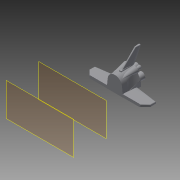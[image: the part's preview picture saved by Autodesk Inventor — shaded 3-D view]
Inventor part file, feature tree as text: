
AUTODESK INVENTOR PART (.ipt)
format: ipt  version: 2015 (Build 190159000, 159)  size: 1,837,568 bytes
history: native  units: in
note: dims shown in document units (in); Inventor stores cm internally (conversion verified against a paired STEP export)
features: sketch x29, plane x15, loft x11, extrude x9, fillet x6, other x3, projected_geometry x3, mirror x2, chamfer x2
ambient origin geometry x8: Origin, YZ Plane, XZ Plane, XY Plane, X Axis, Y Axis, Z Axis, Center Point
bodies: Solid1 (feature_tree)
feature tree (80):
  extrude  "Extrusion1"  TaperAngle=0.0deg  [1 undecoded]
  plane  "Work Plane1"
  plane  "Work Plane2"
  plane  "Work Plane3"
  loft  "Loft1"
  loft  "Loft2"
  fillet  "Fillet1"  Radius=240.6614in
  loft  "Loft4"
  fillet  "Fillet2"  Radius=125.0in
  extrude  "Extrusion2"  TaperAngle=0.0deg  [1 undecoded]
  extrude  "Extrusion3"  Depth=100.0in
  fillet  "Fillet3"  [1 undecoded]
  plane  "Work Plane4"
  mirror  "Mirror1"
  plane  "Work Plane5"
  sketch  "Sketch12"  dims[d36=0.0in d37=90.0deg d38=125.0in]
  loft  "Loft5"
  chamfer  "Chamfer1"  Angle=90.0deg  [1 undecoded]
  chamfer  "Chamfer2"  Angle=90.0deg  [1 undecoded]
  sketch  "Sketch15"  dims[d39=15.0in]
  plane  "Work Plane6"
  plane  "Work Plane7"
  loft  "Loft8"
  mirror  "Mirror2"
  extrude  "Extrusion5"  Depth=125.0in
  extrude  "Extrusion6"  TaperAngle=0.0deg  [1 undecoded]
  plane  "Work Plane8"
  sketch  "Sketch20"  dims[d51=10.0in]
  plane  "Work Plane10"
  loft  "Loft9"
  fillet  "Fillet4"  Radius=84.0in
  extrude  "Extrusion7"  Depth=0.6803in
  fillet  "Fillet5"  Radius=48.0in
  fillet  "Fillet6"  Radius=6500.0in
  sketch  "Sketch23"  dims[d55=0.0in]
  plane  "Work Plane11"
  sketch  "Sketch24"  dims[d56=0.0in]
  loft  "Loft10"
  loft  "Loft11"
  sketch  "Sketch27"  dims[d64=60.0in d70=125.0in]
  plane  "Work Plane12"
  loft  "Loft12"
  loft  "Loft13"
  loft  "Loft14"
  sketch  "Sketch31"  dims[d89=6500.0in d90=7700.0in]
  plane  "Work Plane13"
  sketch  "Sketch32"  dims[d91=10.0in d92=345.0in d93=0.0in]
  sketch  "Sketch33"  dims[d94=10.0in d95=125.0in]
  plane  "Work Plane14"
  extrude  "Extrusion8"  Depth=245.0in
  sketch  "Sketch35"  dims[d98=10.0in d99=0.0in]
  plane  "Work Plane15"
  extrude  "Extrusion9"  Depth=15.0in
  plane  "Work Plane16"
  extrude  "Extrusion10"  Depth=0.0618in
  sketch  "Sketch1"  dims[d5=250.0in d12=0.0in]
  sketch  "Sketch2"  dims[d13=75.0in d15=110.0in]
  other  "Edges1"
  sketch  "Sketch3"  dims[d21=98.0in d24=110.0in d25=240.6614in]
  sketch  "Sketch6"  dims[d26=730.0in d27=0.0in d28=300.0in d29=125.0in]
  sketch  "Sketch7"  dims[d30=250.0in d31=0.0in]
  other  "Edges3"
  sketch  "Sketch8"  dims[d32=125.0in d33=100.0in d34=0.0in d35=90.0deg]
  other  "Edges4"
  sketch  "Sketch17"  dims[d40=20.0in]
  sketch  "Sketch18"  dims[d41=10.0in]
  sketch  "Sketch19"  dims[d50=15.0in]
  projected_geometry  "Projected Loop7"
  sketch  "Sketch21"  dims[d52=75.0in]
  sketch  "Sketch22"  dims[d54=125.0in]
  sketch  "Sketch25"  dims[d57=0.0in d58=0.0in d59=90.0deg d60=0.0in d61=90.0deg]
  sketch  "Sketch26"  dims[d62=10.65in d63=50.0in]
  sketch  "Sketch28"  dims[d71=50.0in d72=0.0in d73=90.0deg]
  sketch  "Sketch29"  dims[d74=0.0in d75=90.0deg d76=40.0in d79=84.0in]
  sketch  "Sketch30"  dims[d80=0.0in d82=0.6803in d83=48.0in d84=0.0in d85=6500.0in]
  sketch  "Sketch34"  dims[d96=200.0in d97=0.0in]
  projected_geometry  "Projected Loop8"
  projected_geometry  "Projected Loop9"
  sketch  "Sketch36"  dims[d100=0.0in d101=245.0in]
  sketch  "Sketch37"  dims[d102=90.0in d105=15.0in d106=0.0618in d107=45.0deg d108=345.0in d109=0.0in d110=90.0deg d111=0.0in d112=90.0deg d113=5.2in d114=0.125in d115=45.0deg d116=5.2in d117=0.125in d118=45.0deg d119=-200.0in d126=100.0in d127=25.0in d133=-205.0in d134=50.0in d135=60.0in d137=0.0in d138=90.0deg d139=0.0in d140=90.0deg d141=160.0in d142=100.0in d143=0.6528in d144=0.0in d145=0.0in d146=9000.0in d147=0.0in d148=15.0in d149=25.0in d150=0.0in d151=30.0in d152=0.0in d153=-20.0in d154=30.0in d155=10.0in d156=1.2162in d157=1.2162in d158=195.0in d160=225.0in d166=30.0in d167=225.0in d168=20.0in d169=30.0in d170=20.0in d171=80.0in d172=0.0in d173=90.0deg d174=0.0in d175=90.0deg d176=7.0in d177=0.1374in d178=200.0in d179=0.0in d180=9.475in d184=150.0in d185=150.0in d186=9.475in d187=40.0in d188=80.0in d189=65.0in d190=60.0in d191=20.0in d192=125.0in d193=0.0in d194=13.0in d195=32.0in d196=55.0in d197=55.0in d198=55.0in d199=80.0in d200=95.0in d201=95.0in d202=40.0in d203=0.0in d204=90.0deg d205=0.0in d206=90.0deg d207=0.0in d208=90.0deg d209=0.0in d210=90.0deg d211=25.0in d212=90.0in d213=8.0in d214=0.0in d215=90.0deg d216=0.0in d217=90.0deg d218=105.0in d219=5.0in d220=5.0in d221=0.0in d222=90.0deg d223=0.0in d224=90.0deg d225=105.0in d226=5.0in d227=5.0in d228=0.0in d229=90.0deg d230=0.0in d231=90.0deg d232=-20.0in d233=90.0deg d234=95.0in d235=0.0in d236=90.0deg d237=105.0in d238=0.0in d239=500.0in d240=1150.0in d241=0.0in]
note: 6 required parameter values undecoded (feature->parameter linkage not recoverable at this tier; creation-order binding heuristic only, values carry confidence <= 0.55)
